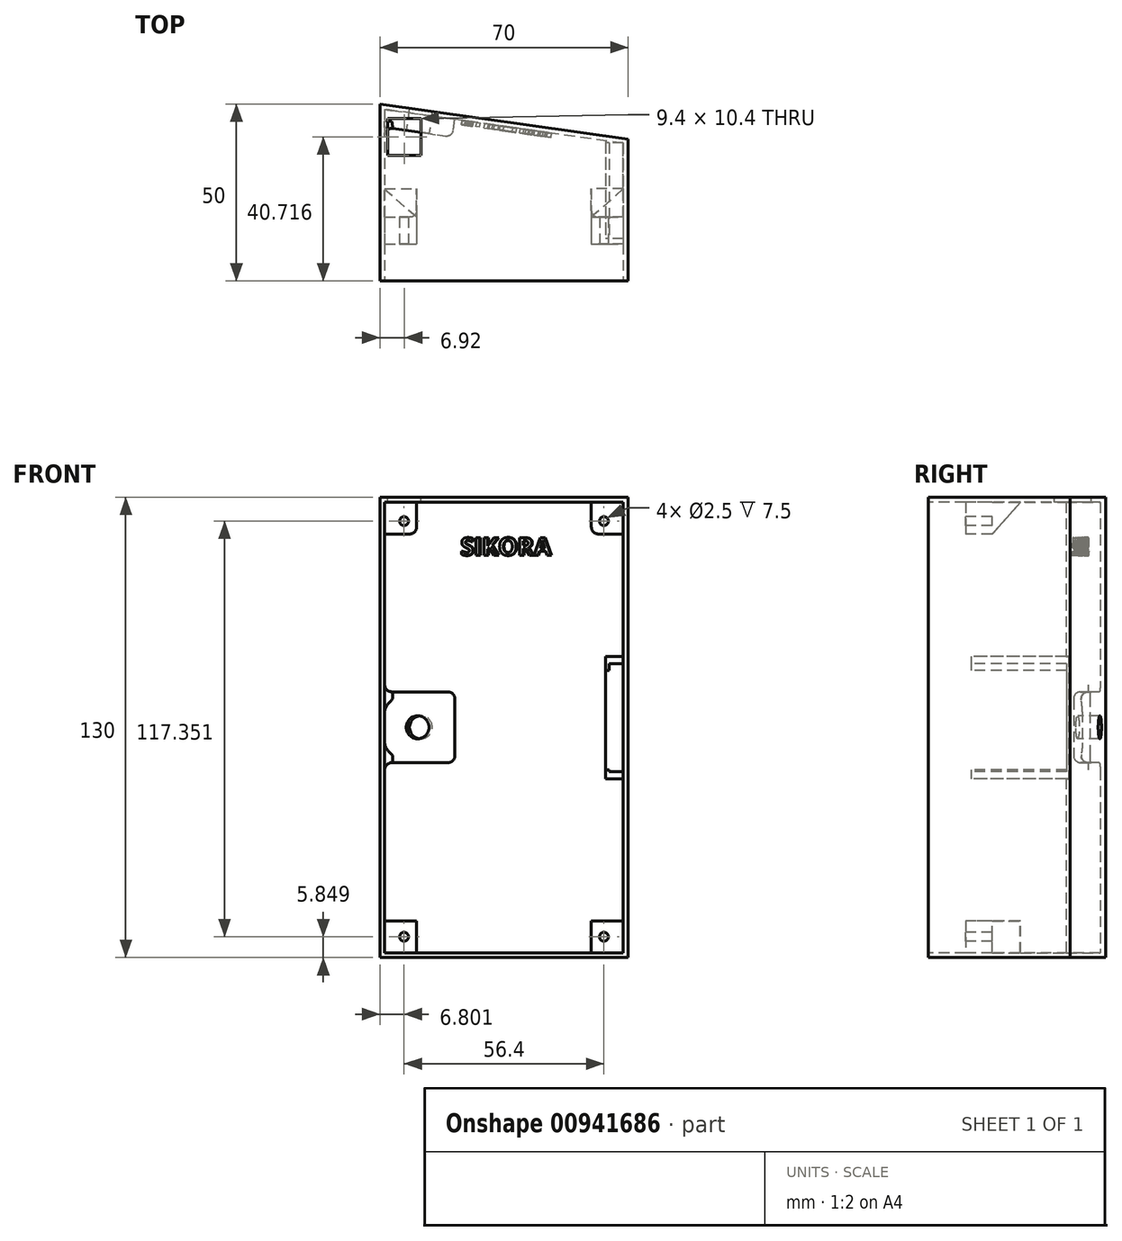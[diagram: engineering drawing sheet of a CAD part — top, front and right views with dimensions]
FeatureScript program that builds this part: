
annotation { "Feature Type Name" : "Feature", "Feature Type Description" : "" }
export const myFeature = defineFeature(function(context is Context, id is Id, definition is map)
    precondition{}
    {
        {
            var Q0;
            Q0=qCreatedBy(makeId("Top.planeOp"),FACE);
            var sketch = newSketch(context, id + "F0", { "sketchPlane" : qUnion([Q0])});
            skLineSegment(sketch, "E0", {"start": v(-43.03, 10) * mm, "end": v(-43.03, -40) * mm});
            skLineSegment(sketch, "E1", {"start": v(-43.03, -40) * mm, "end": v(26.97, -40) * mm});
            skLineSegment(sketch, "E2", {"start": v(26.97, -40) * mm, "end": v(26.97, 0) * mm});
            skLineSegment(sketch, "E3", {"start": v(26.97, 0) * mm, "end": v(-43.03, 10) * mm});
            skSolve(sketch);
        }
        {
            var Q0;
            Q0 = qSketchRegion(id + "F0", true);
            extrude(context, id + "F1", {"entities" : qUnion([Q0]), "depth" : 128.65 * mm, "offsetDistance" : 25 * mm});
        }
        {
            var Q0;
            Q0=makeQuery(id+"F1.opExtrude","CAP_FACE",FACE,{"disambiguationData":[OSD([sQuery(id+"F0.wireOp",EDGE,"E0"),sQuery(id+"F0.wireOp",EDGE,"E1"),sQuery(id+"F0.wireOp",EDGE,"E2"),sQuery(id+"F0.wireOp",EDGE,"E3")])],"isStart":true});
            extrude(context, id + "F2", {"entities" : qUnion([Q0]), "operationType" : NewBodyOperationType.ADD, "depth" : 1.35 * mm, "offsetDistance" : 25 * mm});
        }
        {
            var Q0;
            Q0=qCreatedBy(makeId("Top.planeOp"),FACE);
            var sketch = newSketch(context, id + "F3", { "sketchPlane" : qUnion([Q0])});
            skLineSegment(sketch, "E4.0", {"start": v(-41.68, 8.44) * mm, "end": v(-41.68, -40) * mm});
            skLineSegment(sketch, "E4.1", {"start": v(25.62, -1.17) * mm, "end": v(-41.68, 8.44) * mm});
            skLineSegment(sketch, "E4.2", {"start": v(25.62, -40) * mm, "end": v(25.62, -1.17) * mm});
            skLineSegment(sketch, "E4.3", {"start": v(-41.68, -40) * mm, "end": v(25.62, -40) * mm});
            skSolve(sketch);
        }
        {
            var Q0;
            Q0 = qSketchRegion(id + "F3", true);
            extrude(context, id + "F4", {"entities" : qUnion([Q0]), "operationType" : NewBodyOperationType.REMOVE, "depth" : 127.2 * mm, "offsetDistance" : 25 * mm});
        }
        {
            var Q0;
            {var subQ0=sQuery(id+"F0.wireOp",EDGE,"E1");Q0=makeQuery(id+"F2.boolean.opBoolean","MERGE",FACE,{"derivedFrom":[makeQuery(id+"F1.opExtrude","SWEPT_FACE",FACE,{"disambiguationData":[OSD([subQ0])]}),makeQuery(id+"F2.opExtrude","SWEPT_FACE",FACE,{"disambiguationData":[OSD([subQ0])]})]});}
            var sketch = newSketch(context, id + "F5", { "sketchPlane" : qUnion([Q0])});
            skLineSegment(sketch, "E5.bottom", {"start": v(-41.68, 127.2) * mm, "end": v(-32.68, 127.2) * mm});
            skLineSegment(sketch, "E5.top", {"start": v(-41.68, 118.2) * mm, "end": v(-32.68, 118.2) * mm});
            skLineSegment(sketch, "E5.left", {"start": v(-41.68, 127.2) * mm, "end": v(-41.68, 118.2) * mm});
            skLineSegment(sketch, "E5.right", {"start": v(-32.68, 127.2) * mm, "end": v(-32.68, 118.2) * mm});
            skLineSegment(sketch, "E6.bottom", {"start": v(25.62, 127.2) * mm, "end": v(16.62, 127.2) * mm});
            skLineSegment(sketch, "E6.top", {"start": v(25.62, 118.2) * mm, "end": v(16.62, 118.2) * mm});
            skLineSegment(sketch, "E6.left", {"start": v(25.62, 127.2) * mm, "end": v(25.62, 118.2) * mm});
            skLineSegment(sketch, "E6.right", {"start": v(16.62, 127.2) * mm, "end": v(16.62, 118.2) * mm});
            skLineSegment(sketch, "E7.bottom", {"start": v(-41.68, 0) * mm, "end": v(-32.68, 0) * mm});
            skLineSegment(sketch, "E7.top", {"start": v(-41.68, 9) * mm, "end": v(-32.68, 9) * mm});
            skLineSegment(sketch, "E7.left", {"start": v(-41.68, 0) * mm, "end": v(-41.68, 9) * mm});
            skLineSegment(sketch, "E7.right", {"start": v(-32.68, 0) * mm, "end": v(-32.68, 9) * mm});
            skLineSegment(sketch, "E8.bottom", {"start": v(25.62, 0) * mm, "end": v(16.62, 0) * mm});
            skLineSegment(sketch, "E8.top", {"start": v(25.62, 9) * mm, "end": v(16.62, 9) * mm});
            skLineSegment(sketch, "E8.left", {"start": v(25.62, 0) * mm, "end": v(25.62, 9) * mm});
            skLineSegment(sketch, "E8.right", {"start": v(16.62, 0) * mm, "end": v(16.62, 9) * mm});
            skCircle(sketch, "E9", {"center": v(20.17, 121.85) * mm, "radius": 1.25 * mm});
            skPoint(sketch, "E9.centerSnap0", {"position": v(21.12, 127.2) * mm});
            skCircle(sketch, "E10", {"center": v(-36.23, 121.85) * mm, "radius": 1.25 * mm});
            skCircle(sketch, "E11", {"center": v(-36.23, 4.5) * mm, "radius": 1.25 * mm});
            skCircle(sketch, "E12", {"center": v(20.17, 4.5) * mm, "radius": 1.25 * mm});
            skSolve(sketch);
        }
        {
            var Q0;
            Q0 = qSketchRegion(id + "F5", true);
            extrude(context, id + "F6", {"entities" : qUnion([Q0]), "operationType" : NewBodyOperationType.ADD, "oppositeDirection" : true, "depth" : 18 * mm, "offsetDistance" : 25 * mm});
        }
        {
            var Q0;
            Q0 = qSketchRegion(id + "F5", true);
            extrude(context, id + "F7", {"entities" : qUnion([Q0]), "operationType" : NewBodyOperationType.REMOVE, "oppositeDirection" : true, "depth" : 10.5 * mm, "offsetDistance" : 25 * mm});
        }
        {
            var Q0;
            Q0=makeQuery(id+"F4.boolean.opBoolean","COPY",FACE,{"derivedFrom":makeQuery(id+"F4.opExtrude","SWEPT_FACE",FACE,{"disambiguationData":[OSD([sQuery(id+"F3.wireOp",EDGE,"E4.1")])]})});
            var sketch = newSketch(context, id + "F8", { "sketchPlane" : qUnion([Q0])});
            skLineSegment(sketch, "E13.bottom", {"start": v(-42.45, 53.65) * mm, "end": v(-22.45, 53.65) * mm});
            skLineSegment(sketch, "E13.top", {"start": v(-42.45, 73.65) * mm, "end": v(-22.45, 73.65) * mm});
            skLineSegment(sketch, "E13.left", {"start": v(-42.45, 53.65) * mm, "end": v(-42.45, 73.65) * mm});
            skLineSegment(sketch, "E13.right", {"start": v(-22.45, 53.65) * mm, "end": v(-22.45, 73.65) * mm});
            skSolve(sketch);
        }
        {
            var Q0;
            Q0=makeQuery(id+"F8.imprint","IMPRINT",FACE,{"disambiguationData":[TD([[makeQuery(id+"F8.imprint","IMPRINT",EDGE,{"derivedFrom":sQuery(id+"F8.wireOp",EDGE,"E13.bottom")}),1.0]])]});
            extrude(context, id + "F9", {"entities" : qUnion([Q0]), "operationType" : NewBodyOperationType.ADD, "depth" : 5 * mm, "offsetDistance" : 25 * mm});
        }
        {
            var Q0;
            Q0=makeQuery(id+"F9.opExtrude","CAP_EDGE",EDGE,{"disambiguationData":[OSD([sQuery(id+"F8.wireOp",EDGE,"E13.bottom")])],"isStart":true});
            var Q1;
            Q1=makeQuery(id+"F9.opExtrude","CAP_EDGE",EDGE,{"disambiguationData":[OSD([sQuery(id+"F8.wireOp",EDGE,"E13.right")])],"isStart":true});
            var Q2;
            Q2=makeQuery(id+"F9.opExtrude","CAP_EDGE",EDGE,{"disambiguationData":[OSD([sQuery(id+"F8.wireOp",EDGE,"E13.top")])],"isStart":true});
            var Q3;
            Q3=makeQuery(id+"F9.opExtrude","SWEPT_EDGE",EDGE,{"disambiguationData":[OSD([sQuery(id+"F8.wireOp",EDGE,"E13.top"),sQuery(id+"F8.wireOp",EDGE,"E13.right")])]});
            var Q4;
            Q4=makeQuery(id+"F9.opExtrude","SWEPT_EDGE",EDGE,{"disambiguationData":[OSD([sQuery(id+"F8.wireOp",EDGE,"E13.bottom"),sQuery(id+"F8.wireOp",EDGE,"E13.right")])]});
            var Q5;
            Q5=makeQuery(id+"F9.boolean.opBoolean","INTERSECT",EDGE,{"derivedFrom":[makeQuery(id+"F7.boolean.opBoolean","MERGE",FACE,{"derivedFrom":[makeQuery(id+"F4.boolean.opBoolean","COPY",FACE,{"derivedFrom":makeQuery(id+"F4.opExtrude","SWEPT_FACE",FACE,{"disambiguationData":[OSD([sQuery(id+"F3.wireOp",EDGE,"E4.0")])]})})],"fromTools":[makeQuery(id+"F7.opExtrude","SWEPT_FACE",FACE,{"disambiguationData":[OSD([sQuery(id+"F5.wireOp",EDGE,"E5.left")])]}),makeQuery(id+"F7.opExtrude","SWEPT_FACE",FACE,{"disambiguationData":[OSD([sQuery(id+"F5.wireOp",EDGE,"E7.left")])]})]}),makeQuery(id+"F9.opExtrude","SWEPT_FACE",FACE,{"disambiguationData":[OSD([sQuery(id+"F8.wireOp",EDGE,"E13.bottom")])]})]});
            var Q6;
            Q6=makeQuery(id+"F9.boolean.opBoolean","INTERSECT",EDGE,{"derivedFrom":[makeQuery(id+"F7.boolean.opBoolean","MERGE",FACE,{"derivedFrom":[makeQuery(id+"F4.boolean.opBoolean","COPY",FACE,{"derivedFrom":makeQuery(id+"F4.opExtrude","SWEPT_FACE",FACE,{"disambiguationData":[OSD([sQuery(id+"F3.wireOp",EDGE,"E4.0")])]})})],"fromTools":[makeQuery(id+"F7.opExtrude","SWEPT_FACE",FACE,{"disambiguationData":[OSD([sQuery(id+"F5.wireOp",EDGE,"E5.left")])]}),makeQuery(id+"F7.opExtrude","SWEPT_FACE",FACE,{"disambiguationData":[OSD([sQuery(id+"F5.wireOp",EDGE,"E7.left")])]})]}),makeQuery(id+"F9.opExtrude","SWEPT_FACE",FACE,{"disambiguationData":[OSD([sQuery(id+"F8.wireOp",EDGE,"E13.top")])]})]});
            var Q7;
            Q7=makeQuery(id+"F9.opExtrude","CAP_EDGE",EDGE,{"disambiguationData":[OSD([sQuery(id+"F8.wireOp",EDGE,"E13.top")])],"isStart":false});
            var Q8;
            Q8=makeQuery(id+"F9.opExtrude","CAP_EDGE",EDGE,{"disambiguationData":[OSD([sQuery(id+"F8.wireOp",EDGE,"E13.right")])],"isStart":false});
            var Q9;
            Q9=makeQuery(id+"F9.opExtrude","CAP_EDGE",EDGE,{"disambiguationData":[OSD([sQuery(id+"F8.wireOp",EDGE,"E13.bottom")])],"isStart":false});
            fillet(context, id + "F10", {"entities" : qUnion([Q0, Q1, Q2, Q3, Q4, Q5, Q6, Q7, Q8, Q9]), "radius" : 2 * mm, "tangentPropagation" : true, "allowEdgeOverflow" : false});
        }
        {
            var Q0;
            Q0=makeQuery(id+"F9.opExtrude","CAP_FACE",FACE,{"disambiguationData":[OSD([sQuery(id+"F8.wireOp",EDGE,"E13.bottom"),sQuery(id+"F8.wireOp",EDGE,"E13.top"),sQuery(id+"F8.wireOp",EDGE,"E13.left"),sQuery(id+"F8.wireOp",EDGE,"E13.right")])],"isStart":false});
            var sketch = newSketch(context, id + "F11", { "sketchPlane" : qUnion([Q0])});
            skCircle(sketch, "E14", {"center": v(-32.35, 63.65) * mm, "radius": 3.25 * mm});
            skSolve(sketch);
        }
        {
            var Q0;
            Q0=makeQuery(id+"F11.imprint","IMPRINT",FACE,{"disambiguationData":[TD([[makeQuery(id+"F11.imprint","IMPRINT",EDGE,{"derivedFrom":sQuery(id+"F11.wireOp",EDGE,"E14")}),1.0]])]});
            extrude(context, id + "F12", {"entities" : qUnion([Q0]), "operationType" : NewBodyOperationType.REMOVE, "oppositeDirection" : true, "depth" : 25 * mm, "offsetDistance" : 25 * mm});
        }
        {
            var Q0;
            Q0=makeQuery(id+"F4.boolean.opBoolean","COPY",FACE,{"derivedFrom":makeQuery(id+"F4.opExtrude","SWEPT_FACE",FACE,{"disambiguationData":[OSD([sQuery(id+"F3.wireOp",EDGE,"E4.1")])]})});
            var sketch = newSketch(context, id + "F13", { "sketchPlane" : qUnion([Q0])});
            skText(sketch, "E15", { "text": "SIKORA", "fontName": "OpenSans-Bold.ttf"});
            const initialGuessF13  = {"E15": [-0.0207, 0.1122, 1, 0, 0.005]};
            skSetInitialGuess(sketch, initialGuessF13);
            skSolve(sketch);
        }
        {
            var Q0;
            Q0 = qSketchRegion(id + "F13", true);
            extrude(context, id + "F14", {"entities" : qUnion([Q0]), "operationType" : NewBodyOperationType.ADD, "depth" : 1.2 * mm, "offsetDistance" : 25 * mm});
        }
        {
            var Q0;
            {var subQ0=sQuery(id+"F0.wireOp",EDGE,"E1");Q0=makeQuery(id+"F6.boolean.opBoolean","MERGE",FACE,{"derivedFrom":[makeQuery(id+"F2.boolean.opBoolean","MERGE",FACE,{"derivedFrom":[makeQuery(id+"F1.opExtrude","SWEPT_FACE",FACE,{"disambiguationData":[OSD([subQ0])]}),makeQuery(id+"F2.opExtrude","SWEPT_FACE",FACE,{"disambiguationData":[OSD([subQ0])]})]}),makeQuery(id+"F6.opExtrude","CAP_FACE",FACE,{"disambiguationData":[OSD([sQuery(id+"F5.wireOp",EDGE,"E5.bottom"),sQuery(id+"F5.wireOp",EDGE,"E5.top"),sQuery(id+"F5.wireOp",EDGE,"E5.left"),sQuery(id+"F5.wireOp",EDGE,"E5.right"),sQuery(id+"F5.wireOp",EDGE,"E10")])],"isStart":true}),makeQuery(id+"F6.opExtrude","CAP_FACE",FACE,{"disambiguationData":[OSD([sQuery(id+"F5.wireOp",EDGE,"E6.bottom"),sQuery(id+"F5.wireOp",EDGE,"E6.top"),sQuery(id+"F5.wireOp",EDGE,"E6.left"),sQuery(id+"F5.wireOp",EDGE,"E6.right"),sQuery(id+"F5.wireOp",EDGE,"E9")])],"isStart":true}),makeQuery(id+"F6.opExtrude","CAP_FACE",FACE,{"disambiguationData":[OSD([sQuery(id+"F5.wireOp",EDGE,"E7.bottom"),sQuery(id+"F5.wireOp",EDGE,"E7.top"),sQuery(id+"F5.wireOp",EDGE,"E7.left"),sQuery(id+"F5.wireOp",EDGE,"E7.right"),sQuery(id+"F5.wireOp",EDGE,"E11")])],"isStart":true}),makeQuery(id+"F6.opExtrude","CAP_FACE",FACE,{"disambiguationData":[OSD([sQuery(id+"F5.wireOp",EDGE,"E8.bottom"),sQuery(id+"F5.wireOp",EDGE,"E8.top"),sQuery(id+"F5.wireOp",EDGE,"E8.left"),sQuery(id+"F5.wireOp",EDGE,"E8.right"),sQuery(id+"F5.wireOp",EDGE,"E12")])],"isStart":true})]});}
            var sketch = newSketch(context, id + "F15", { "sketchPlane" : qUnion([Q0])});
            skLineSegment(sketch, "E16.bottom", {"start": v(25.62, 83.65) * mm, "end": v(20.62, 83.65) * mm});
            skLineSegment(sketch, "E16.top", {"start": v(25.62, 49.15) * mm, "end": v(20.62, 49.15) * mm});
            skLineSegment(sketch, "E16.left", {"start": v(25.62, 83.65) * mm, "end": v(25.62, 49.15) * mm});
            skLineSegment(sketch, "E16.right", {"start": v(20.62, 83.65) * mm, "end": v(20.62, 49.15) * mm});
            skSolve(sketch);
        }
        {
            var Q0;
            Q0=makeQuery(id+"F15.imprint","IMPRINT",FACE,{"disambiguationData":[TD([[makeQuery(id+"F15.imprint","IMPRINT",EDGE,{"derivedFrom":sQuery(id+"F15.wireOp",EDGE,"E16.bottom")}),1.0]])]});
            extrude(context, id + "F16", {"entities" : qUnion([Q0]), "operationType" : NewBodyOperationType.ADD, "oppositeDirection" : true, "depth" : 40 * mm, "offsetDistance" : 25 * mm, "hasSecondDirection" : true, "secondDirectionOppositeDirection" : true, "secondDirectionDepth" : 12 * mm});
        }
        {
            var Q0;
            Q0=makeQuery(id+"F16.opExtrude","CAP_FACE",FACE,{"disambiguationData":[OSD([sQuery(id+"F15.wireOp",EDGE,"E16.bottom"),sQuery(id+"F15.wireOp",EDGE,"E16.top"),sQuery(id+"F15.wireOp",EDGE,"E16.left"),sQuery(id+"F15.wireOp",EDGE,"E16.right")])],"isStart":true});
            var sketch = newSketch(context, id + "F17", { "sketchPlane" : qUnion([Q0])});
            skLineSegment(sketch, "E17", {"start": v(25.62, 81.65) * mm, "end": v(21.62, 81.65) * mm});
            skLineSegment(sketch, "E18", {"start": v(21.62, 81.65) * mm, "end": v(21.62, 79.65) * mm});
            skLineSegment(sketch, "E19", {"start": v(21.62, 79.65) * mm, "end": v(20.62, 79.65) * mm});
            skLineSegment(sketch, "E20", {"start": v(20.62, 79.65) * mm, "end": v(20.62, 51.65) * mm});
            skLineSegment(sketch, "E21", {"start": v(20.62, 51.65) * mm, "end": v(21.62, 51.65) * mm});
            skLineSegment(sketch, "E22", {"start": v(21.62, 51.65) * mm, "end": v(21.62, 51.15) * mm});
            skLineSegment(sketch, "E23", {"start": v(21.62, 51.15) * mm, "end": v(25.62, 51.15) * mm});
            skLineSegment(sketch, "E24", {"start": v(25.62, 51.15) * mm, "end": v(25.62, 81.65) * mm});
            skSolve(sketch);
        }
        {
            var Q0;
            Q0=makeQuery(id+"F17.imprint","IMPRINT",FACE,{"disambiguationData":[TD([[makeQuery(id+"F17.imprint","IMPRINT",EDGE,{"derivedFrom":sQuery(id+"F17.wireOp",EDGE,"E17")}),1.0]])]});
            extrude(context, id + "F18", {"entities" : qUnion([Q0]), "operationType" : NewBodyOperationType.REMOVE, "oppositeDirection" : true, "depth" : 27 * mm, "offsetDistance" : 25 * mm});
        }
        {
            var Q0;
            Q0=makeQuery(id+"F6.opExtrude","SWEPT_FACE",FACE,{"disambiguationData":[OSD([sQuery(id+"F5.wireOp",EDGE,"E6.right")])]});
            var sketch = newSketch(context, id + "F19", { "sketchPlane" : qUnion([Q0])});
            skLineSegment(sketch, "E25", {"start": v(22, 118.2) * mm, "end": v(14, 127.18) * mm});
            skLineSegment(sketch, "E26", {"start": v(14, 127.18) * mm, "end": v(22, 127.2) * mm});
            skLineSegment(sketch, "E27", {"start": v(22, 127.2) * mm, "end": v(22, 118.2) * mm});
            skSolve(sketch);
        }
        {
            var Q0;
            Q0=makeQuery(id+"F19.imprint","IMPRINT",FACE,{"disambiguationData":[TD([[makeQuery(id+"F19.imprint","IMPRINT",EDGE,{"derivedFrom":sQuery(id+"F19.wireOp",EDGE,"E25")}),-1.0]])]});
            extrude(context, id + "F20", {"entities" : qUnion([Q0]), "operationType" : NewBodyOperationType.ADD, "oppositeDirection" : true, "depth" : 9 * mm, "offsetDistance" : 25 * mm});
        }
        {
            var Q0;
            Q0=makeQuery(id+"F6.opExtrude","SWEPT_FACE",FACE,{"disambiguationData":[OSD([sQuery(id+"F5.wireOp",EDGE,"E5.right")])]});
            var sketch = newSketch(context, id + "F21", { "sketchPlane" : qUnion([Q0])});
            skLineSegment(sketch, "E28", {"start": v(-22, 127.2) * mm, "end": v(-22, 118.2) * mm});
            skLineSegment(sketch, "E29", {"start": v(-22, 118.2) * mm, "end": v(-14, 127.2) * mm});
            skLineSegment(sketch, "E30", {"start": v(-14, 127.2) * mm, "end": v(-22, 127.2) * mm});
            skSolve(sketch);
        }
        {
            var Q0;
            Q0=makeQuery(id+"F21.imprint","IMPRINT",FACE,{"disambiguationData":[TD([[makeQuery(id+"F21.imprint","IMPRINT",EDGE,{"derivedFrom":sQuery(id+"F21.wireOp",EDGE,"E28")}),1.0]])]});
            extrude(context, id + "F22", {"entities" : qUnion([Q0]), "operationType" : NewBodyOperationType.ADD, "oppositeDirection" : true, "depth" : 9 * mm, "offsetDistance" : 25 * mm});
        }
        {
            var Q0;
            Q0=makeQuery(id+"F6.opExtrude","SWEPT_EDGE",EDGE,{"disambiguationData":[OSD([sQuery(id+"F5.wireOp",EDGE,"E5.top"),sQuery(id+"F5.wireOp",EDGE,"E5.right")])]});
            var Q1;
            Q1=makeQuery(id+"F6.opExtrude","SWEPT_EDGE",EDGE,{"disambiguationData":[OSD([sQuery(id+"F5.wireOp",EDGE,"E6.top"),sQuery(id+"F5.wireOp",EDGE,"E6.right")])]});
            var Q2;
            Q2=makeQuery(id+"F6.opExtrude","SWEPT_EDGE",EDGE,{"disambiguationData":[OSD([sQuery(id+"F3.wireOp",EDGE,"E4.2"),sQuery(id+"F3.wireOp",EDGE,"E4.3"),sQuery(id+"F5.wireOp",EDGE,"E6.top"),sQuery(id+"F5.wireOp",EDGE,"E6.left")])]});
            var Q3;
            Q3=makeQuery(id+"F6.opExtrude","SWEPT_EDGE",EDGE,{"disambiguationData":[OSD([sQuery(id+"F3.wireOp",EDGE,"E4.0"),sQuery(id+"F3.wireOp",EDGE,"E4.3"),sQuery(id+"F5.wireOp",EDGE,"E5.top"),sQuery(id+"F5.wireOp",EDGE,"E5.left")])]});
            fillet(context, id + "F23", {"entities" : qUnion([Q0, Q1, Q2, Q3]), "radius" : 2 * mm, "tangentPropagation" : true, "allowEdgeOverflow" : false});
        }
        {
            var Q0;
            Q0=makeQuery(id+"F6.opExtrude","SWEPT_FACE",FACE,{"disambiguationData":[OSD([sQuery(id+"F5.wireOp",EDGE,"E8.top")])]});
            var sketch = newSketch(context, id + "F24", { "sketchPlane" : qUnion([Q0])});
            skLineSegment(sketch, "E31", {"start": v(16.62, -22) * mm, "end": v(25.62, -22) * mm});
            skLineSegment(sketch, "E32", {"start": v(25.62, -22) * mm, "end": v(25.62, -14) * mm});
            skLineSegment(sketch, "E33", {"start": v(25.62, -14) * mm, "end": v(16.62, -22) * mm});
            skSolve(sketch);
        }
        {
            var Q0;
            Q0=makeQuery(id+"F24.imprint","IMPRINT",FACE,{"disambiguationData":[TD([[makeQuery(id+"F24.imprint","IMPRINT",EDGE,{"derivedFrom":sQuery(id+"F24.wireOp",EDGE,"E31")}),-1.0]])]});
            extrude(context, id + "F25", {"entities" : qUnion([Q0]), "operationType" : NewBodyOperationType.ADD, "oppositeDirection" : true, "depth" : 9 * mm, "offsetDistance" : 25 * mm});
        }
        {
            var Q0;
            Q0=makeQuery(id+"F6.opExtrude","SWEPT_FACE",FACE,{"disambiguationData":[OSD([sQuery(id+"F5.wireOp",EDGE,"E7.top")])]});
            var sketch = newSketch(context, id + "F26", { "sketchPlane" : qUnion([Q0])});
            skLineSegment(sketch, "E34", {"start": v(-41.68, -22) * mm, "end": v(-32.68, -22) * mm});
            skLineSegment(sketch, "E35", {"start": v(-32.68, -22) * mm, "end": v(-41.68, -14.13) * mm});
            skLineSegment(sketch, "E36", {"start": v(-41.68, -14.13) * mm, "end": v(-41.68, -22) * mm});
            skSolve(sketch);
        }
        {
            var Q0;
            Q0=makeQuery(id+"F26.imprint","IMPRINT",FACE,{"disambiguationData":[TD([[makeQuery(id+"F26.imprint","IMPRINT",EDGE,{"derivedFrom":sQuery(id+"F26.wireOp",EDGE,"E34")}),1.0]])]});
            extrude(context, id + "F27", {"entities" : qUnion([Q0]), "operationType" : NewBodyOperationType.ADD, "oppositeDirection" : true, "depth" : 9 * mm, "offsetDistance" : 25 * mm});
        }
        {
            var Q0;
            Q0=makeQuery(id+"F1.opExtrude","CAP_FACE",FACE,{"disambiguationData":[OSD([sQuery(id+"F0.wireOp",EDGE,"E0"),sQuery(id+"F0.wireOp",EDGE,"E1"),sQuery(id+"F0.wireOp",EDGE,"E2"),sQuery(id+"F0.wireOp",EDGE,"E3")])],"isStart":false});
            var sketch = newSketch(context, id + "F28", { "sketchPlane" : qUnion([Q0])});
            skLineSegment(sketch, "E37.right", {"start": v(-31.41, 0.05) * mm, "end": v(-31.43, 0) * mm});
            skLineSegment(sketch, "E38", {"start": v(-43.03, 10) * mm, "end": v(36.73, -1.4) * mm, "construction": true});
            skLineSegment(sketch, "E39.bottom", {"start": v(-31.41, 5.92) * mm, "end": v(-40.81, 5.92) * mm});
            skLineSegment(sketch, "E39.top", {"start": v(-31.41, -4.48) * mm, "end": v(-40.81, -4.48) * mm});
            skLineSegment(sketch, "E39.left", {"start": v(-31.41, 5.92) * mm, "end": v(-31.41, -4.48) * mm});
            skLineSegment(sketch, "E39.right", {"start": v(-40.81, 5.92) * mm, "end": v(-40.81, -4.48) * mm});
            skSolve(sketch);
        }
        {
            var Q0;
            {var subQ3=sQuery(id+"F28.wireOp",EDGE,"E39.bottom");Q0=makeQuery(id+"F28.imprint","IMPRINT",FACE,{"disambiguationData":[TD([[makeQuery(id+"F28.imprint","IMPRINT",EDGE,{"derivedFrom":subQ3}),1.0]])]});}
            extrude(context, id + "F29", {"entities" : qUnion([Q0]), "operationType" : NewBodyOperationType.REMOVE, "oppositeDirection" : true, "depth" : 2 * mm, "offsetDistance" : 25 * mm});
        }
    });
